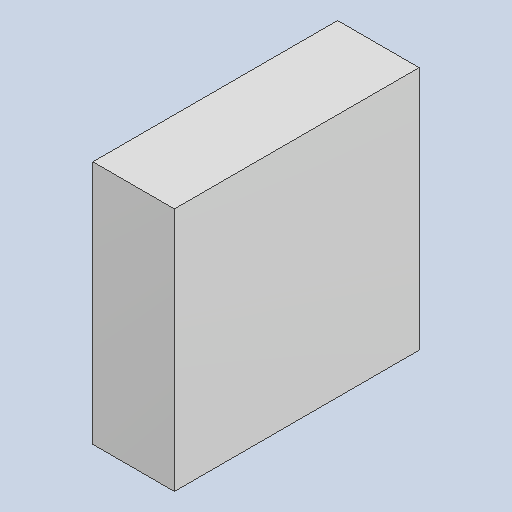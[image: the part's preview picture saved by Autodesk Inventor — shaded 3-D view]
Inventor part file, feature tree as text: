
AUTODESK INVENTOR PART (.ipt)
format: ipt  version: 2023.4 (Build 274418000, 418)  size: 81,408 bytes
history: native  units: mm
features: extrude x1
ambient origin geometry x8: Origin, YZ Plane, XZ Plane, XY Plane, X Axis, Y Axis, Z Axis, Center Point
bodies: Solid1 (feature_tree)
feature tree (1):
  extrude  "Extruded_26"  [1 undecoded]
note: 1 required parameter value undecoded (feature->parameter linkage not recoverable at this tier; creation-order binding heuristic only, values carry confidence <= 0.55)
